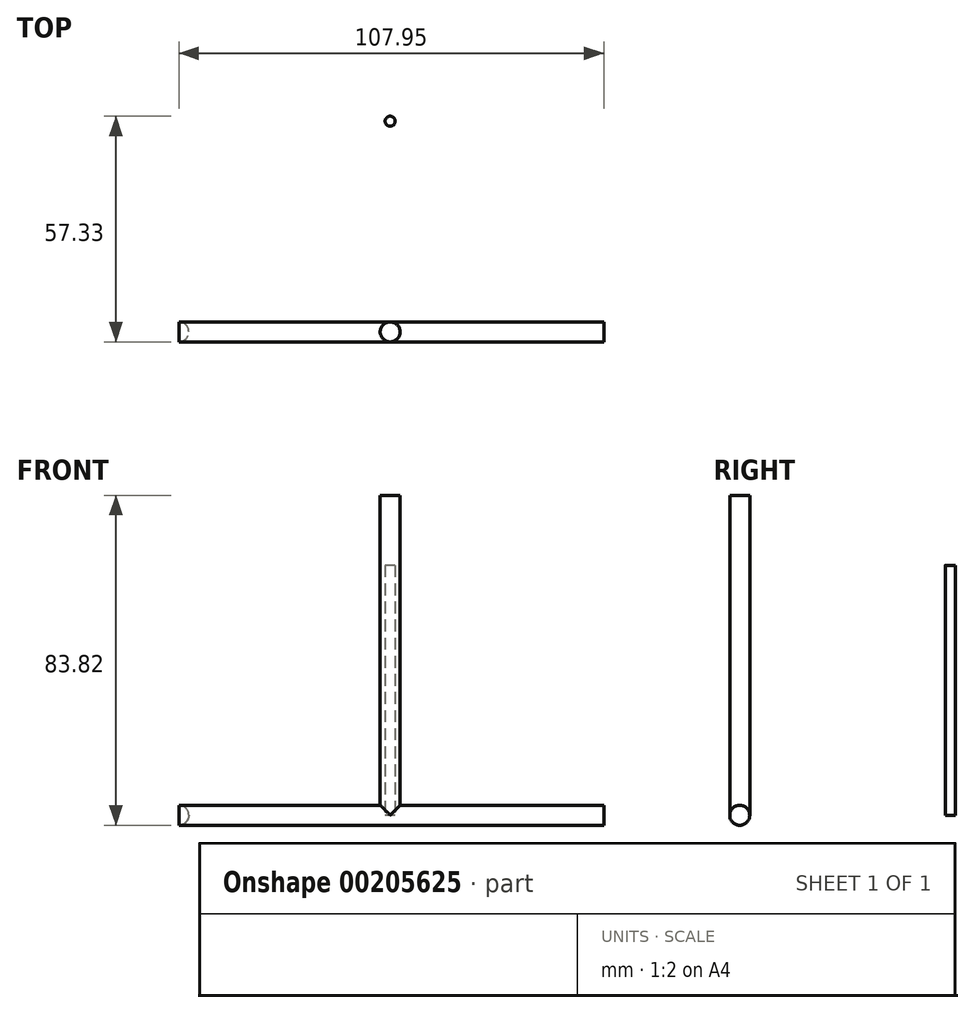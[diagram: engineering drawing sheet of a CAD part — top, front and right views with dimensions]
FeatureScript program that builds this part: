
annotation { "Feature Type Name" : "Feature", "Feature Type Description" : "" }
export const myFeature = defineFeature(function(context is Context, id is Id, definition is map)
    precondition{}
    {
        {
            var Q0;
            Q0=qCreatedBy(makeId("Front.planeOp"),FACE);
            var sketch = newSketch(context, id + "F0", { "sketchPlane" : qUnion([Q0])});
            skLineSegment(sketch, "E0.left", {"start": v(2.54, -40.64) * mm, "end": v(2.54, 40.64) * mm});
            skPoint(sketch, "E0.middle", {"position": v(0, 0) * mm});
            skLineSegment(sketch, "E1.bottom", {"start": v(0, 40.64) * mm, "end": v(2.54, 40.64) * mm});
            skLineSegment(sketch, "E1.top", {"start": v(0, -40.64) * mm, "end": v(2.54, -40.64) * mm});
            skLineSegment(sketch, "E1.left", {"start": v(0, 40.64) * mm, "end": v(0, -40.64) * mm});
            skLineSegment(sketch, "E1.right", {"start": v(2.54, 40.64) * mm, "end": v(2.54, -40.64) * mm});
            skLineSegment(sketch, "E2", {"start": v(53.34, -40.64) * mm, "end": v(-53.34, -40.64) * mm, "construction": true});
            skSolve(sketch);
        }
        {
            var Q0;
            Q0=makeQuery(id+"F0.imprint","IMPRINT",FACE,{"disambiguationData":[TD([[makeQuery(id+"F0.imprint","IMPRINT",EDGE,{"derivedFrom":sQuery(id+"F0.wireOp",EDGE,"E1.bottom")}),-1.0]])]});
            var Q1;
            Q1=sQuery(id+"F0.wireOp",EDGE,"E1.left");
            revolve(context, id + "F1", {"entities" : qUnion([Q0]), "axis" : qUnion([Q1]), "revolveType" : RevolveType.FULL});
        }
        {
            var Q0;
            Q0=qCreatedBy(makeId("Front.planeOp"),FACE);
            var sketch = newSketch(context, id + "F2", { "sketchPlane" : qUnion([Q0])});
            skCircle(sketch, "E3", {"center": v(-53.7, -40.64) * mm, "radius": 2.54 * mm});
            skSolve(sketch);
        }
        {
            var Q0;
            Q0=sQuery(id+"F2.wireOp",EDGE,"E3");
            var Q1;
            Q1=sQuery(id+"F0.wireOp",EDGE,"E1.left");
            revolve(context, id + "F3", {"bodyType" : ToolBodyType.SURFACE, "surfaceEntities" : qUnion([Q0]), "axis" : qUnion([Q1]), "revolveType" : RevolveType.ONE_DIRECTION, "angle" : 180 * degree});
        }
        {
            var Q0;
            Q0=makeQuery(id+"F2.imprint","IMPRINT",FACE,{"disambiguationData":[TD([[makeQuery(id+"F2.imprint","IMPRINT",EDGE,{"derivedFrom":sQuery(id+"F2.wireOp",EDGE,"E3")}),1.0]])]});
            var sketch = newSketch(context, id + "F4", { "sketchPlane" : qUnion([Q0])});
            skLineSegment(sketch, "E4.bottom", {"start": v(-53.7, -40.64) * mm, "end": v(54.26, -40.64) * mm});
            skLineSegment(sketch, "E4.top", {"start": v(-53.7, -43.18) * mm, "end": v(54.26, -43.18) * mm});
            skLineSegment(sketch, "E4.left", {"start": v(-53.7, -40.64) * mm, "end": v(-53.7, -43.18) * mm});
            skLineSegment(sketch, "E4.right", {"start": v(54.26, -40.64) * mm, "end": v(54.26, -43.18) * mm});
            skSolve(sketch);
        }
        {
            var Q0;
            {var subQ4=sQuery(id+"F4.wireOp",EDGE,"E4.top");Q0=makeQuery(id+"F4.imprint","IMPRINT",FACE,{"disambiguationData":[TD([[makeQuery(id+"F4.imprint","IMPRINT",EDGE,{"derivedFrom":subQ4}),1.0]])]});}
            var Q1;
            Q1=sQuery(id+"F4.wireOp",EDGE,"E4.bottom");
            revolve(context, id + "F5", {"operationType" : NewBodyOperationType.ADD, "entities" : qUnion([Q0]), "axis" : qUnion([Q1]), "revolveType" : RevolveType.FULL});
        }
        {
            var Q0;
            Q0=qCreatedBy(makeId("Top.planeOp"),FACE);
            cPlane(context, id + "F6", {"entities" : qUnion([Q0]), "cplaneType" : CPlaneType.OFFSET, "offset" : 40.64 * mm, "oppositeDirection" : true, "width" : 152.4 * mm, "height" : 152.4 * mm});
        }
        {
            var Q0;
            Q0=qCreatedBy(id+"F6.planeOp",FACE);
            var sketch = newSketch(context, id + "F7", { "sketchPlane" : qUnion([Q0])});
            skCircle(sketch, "E5", {"center": v(0, 53.52) * mm, "radius": 1.27 * mm});
            skSolve(sketch);
        }
        {
            var Q0;
            Q0 = qSketchRegion(id + "F7", true);
            extrude(context, id + "F8", {"entities" : qUnion([Q0]), "depth" : 63.5 * mm});
        }
    });
